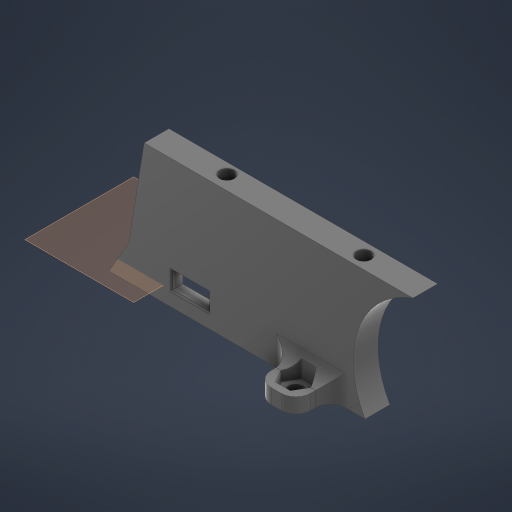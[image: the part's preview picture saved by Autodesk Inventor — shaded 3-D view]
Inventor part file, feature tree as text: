
AUTODESK INVENTOR PART (.ipt)
format: ipt  version: 2024 (Build 280153000, 153)  size: 368,640 bytes
history: native  units: in
note: dims shown in document units (in); Inventor stores cm internally (conversion verified against a paired STEP export)
features: sketch x6, extrude x5, fillet x2, plane x1, chamfer x1, emboss x1
ambient origin geometry x8: Origin, YZ Plane, XZ Plane, XY Plane, X Axis, Y Axis, Z Axis, Center Point
bodies: Solid1 (feature_tree)
feature tree (16):
  extrude  "Extrusion1"  Depth=0.315in
  plane  "Work Plane1"
  extrude  "Extrusion6"  TaperAngle=0.0deg  [1 undecoded]
  chamfer  "Chamfer2"  Distance=0.0984in Angle=45.0deg
  emboss  "Emboss1"
  extrude  "Extrusion8"  Depth=0.1181in TaperAngle=0.0deg
  extrude  "Extrusion9"  Depth=0.0787in TaperAngle=0.0deg
  extrude  "Extrusion10"  Depth=0.1181in
  fillet  "Fillet5"  [1 undecoded]
  fillet  "Fillet6"  [1 undecoded]
  sketch  "Sketch1"  dims[d1=0.1969in d2=0.0in d52=0.315in]
  sketch  "Sketch6"  dims[d53=0.1575in d54=0.0in d55=0.0in d56=0.0984in d57=0.1772in d58=45.0deg]
  sketch  "Sketch9"  dims[d66=0.0394in d67=0.0in d68=0.1181in d69=0.0in]
  sketch  "Sketch10"  dims[d70=0.0787in d71=0.0in d72=0.0787in d73=0.0in]
  sketch  "Sketch11"  dims[d74=0.1181in d75=0.1181in]
  sketch  "Sketch12"
note: 3 required parameter values undecoded (feature->parameter linkage not recoverable at this tier; creation-order binding heuristic only, values carry confidence <= 0.55)
